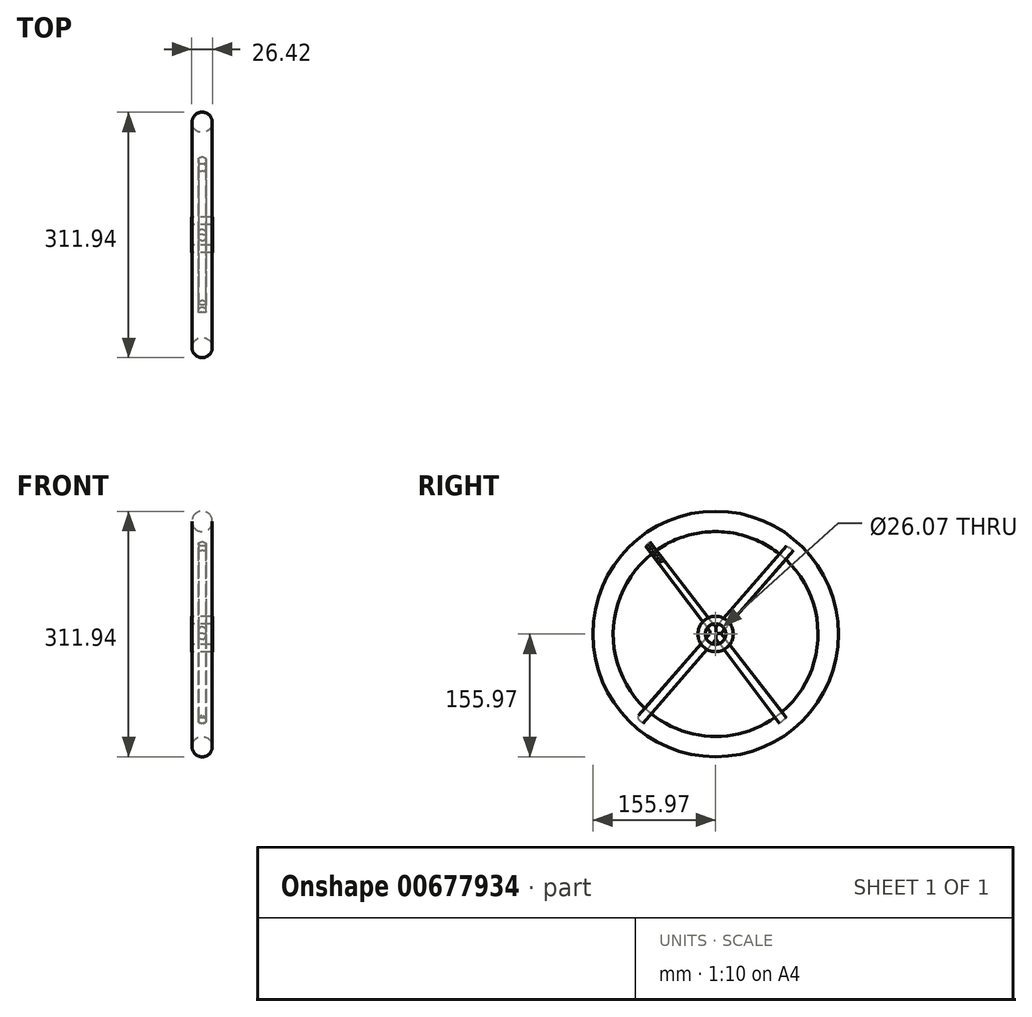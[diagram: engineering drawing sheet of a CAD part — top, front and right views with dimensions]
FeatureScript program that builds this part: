
annotation { "Feature Type Name" : "Feature", "Feature Type Description" : "" }
export const myFeature = defineFeature(function(context is Context, id is Id, definition is map)
    precondition{}
    {
        {
            var Q0;
            Q0=qCreatedBy(makeId("Front.planeOp"),FACE);
            var sketch = newSketch(context, id + "F0", { "sketchPlane" : qUnion([Q0])});
            skLineSegment(sketch, "E0", {"start": v(-177.23, 0) * mm, "end": v(182.9, 0) * mm, "construction": true});
            skCircle(sketch, "E1", {"center": v(0, 143.04) * mm, "radius": 12.92 * mm});
            skSolve(sketch);
        }
        {
            var Q0;
            Q0=makeQuery(id+"F0.imprint","IMPRINT",FACE,{"disambiguationData":[TD([[makeQuery(id+"F0.imprint","IMPRINT",EDGE,{"derivedFrom":sQuery(id+"F0.wireOp",EDGE,"E1")}),1.0]])]});
            var Q1;
            Q1=sQuery(id+"F0.wireOp",EDGE,"E0");
            revolve(context, id + "F1", {"entities" : qUnion([Q0]), "axis" : qUnion([Q1]), "revolveType" : RevolveType.FULL});
        }
        {
            var Q0;
            Q0=qCreatedBy(makeId("Right.planeOp"),FACE);
            var sketch = newSketch(context, id + "F2", { "sketchPlane" : qUnion([Q0])});
            skCircle(sketch, "E2", {"center": v(0, 0) * mm, "radius": 22.46 * mm});
            skCircle(sketch, "E3", {"center": v(0, 0) * mm, "radius": 13.04 * mm});
            skSolve(sketch);
        }
        {
            var Q0;
            Q0 = qSketchRegion(id + "F2", true);
            extrude(context, id + "F3", {"entities" : qUnion([Q0]), "endBound" : BoundingType.SYMMETRIC, "depth" : 26.42 * mm, "offsetDistance" : 25.4 * mm});
        }
        {
            var Q0;
            Q0=qCreatedBy(makeId("Right.planeOp"),FACE);
            var sketch = newSketch(context, id + "F4", { "sketchPlane" : qUnion([Q0])});
            skLineSegment(sketch, "E4", {"start": v(-88.84, 111.85) * mm, "end": v(81, -113.28) * mm});
            skLineSegment(sketch, "E5", {"start": v(81, -113.28) * mm, "end": v(90.1, -106.4) * mm});
            skLineSegment(sketch, "E6", {"start": v(90.1, -106.4) * mm, "end": v(-83.49, 116.85) * mm});
            skLineSegment(sketch, "E7", {"start": v(-83.49, 116.85) * mm, "end": v(-88.84, 111.85) * mm});
            skLineSegment(sketch, "E8", {"start": v(90.1, 111.85) * mm, "end": v(-100.26, -106.4) * mm});
            skLineSegment(sketch, "E9", {"start": v(-100.26, -106.4) * mm, "end": v(-92.37, -113.28) * mm});
            skLineSegment(sketch, "E10", {"start": v(-92.37, -113.28) * mm, "end": v(98.94, 106.05) * mm});
            skLineSegment(sketch, "E11", {"start": v(98.94, 106.05) * mm, "end": v(90.1, 111.85) * mm});
            skSolve(sketch);
        }
        {
            var Q0;
            Q0 = qSketchRegion(id + "F4", true);
            extrude(context, id + "F5", {"entities" : qUnion([Q0]), "endBound" : BoundingType.SYMMETRIC, "depth" : 9.65 * mm, "offsetDistance" : 25.4 * mm});
        }
        {
            var Q0;
            {var subQ0=sQuery(id+"F4.wireOp",EDGE,"E4");Q0=makeQuery(id+"F5.opExtrude","CAP_EDGE",EDGE,{"disambiguationData":[OSD([subQ0]),TDD([makeQuery(id+"F4.imprint","IMPRINT",EDGE,{"disambiguationData":[TD([[makeQuery(id+"F4.imprint","INTERSECT",VERTEX,{"derivedFrom":[subQ0,sQuery(id+"F4.wireOp",EDGE,"E7")]}),-1.0]])],"derivedFrom":subQ0})])],"isStart":false});}
            var Q1;
            {var subQ0=sQuery(id+"F4.wireOp",EDGE,"E4");Q1=makeQuery(id+"F5.opExtrude","CAP_EDGE",EDGE,{"disambiguationData":[OSD([subQ0]),TDD([makeQuery(id+"F4.imprint","IMPRINT",EDGE,{"disambiguationData":[TD([[makeQuery(id+"F4.imprint","INTERSECT",VERTEX,{"derivedFrom":[subQ0,sQuery(id+"F4.wireOp",EDGE,"E7")]}),-1.0]])],"derivedFrom":subQ0})])],"isStart":true});}
            var Q2;
            {var subQ0=sQuery(id+"F4.wireOp",EDGE,"E6");Q2=makeQuery(id+"F5.opExtrude","CAP_EDGE",EDGE,{"disambiguationData":[OSD([subQ0]),TDD([makeQuery(id+"F4.imprint","IMPRINT",EDGE,{"disambiguationData":[TD([[makeQuery(id+"F4.imprint","INTERSECT",VERTEX,{"derivedFrom":[subQ0,sQuery(id+"F4.wireOp",EDGE,"E7")]}),1.0]])],"derivedFrom":subQ0})])],"isStart":false});}
            var Q3;
            {var subQ0=sQuery(id+"F4.wireOp",EDGE,"E6");Q3=makeQuery(id+"F5.opExtrude","CAP_EDGE",EDGE,{"disambiguationData":[OSD([subQ0]),TDD([makeQuery(id+"F4.imprint","IMPRINT",EDGE,{"disambiguationData":[TD([[makeQuery(id+"F4.imprint","INTERSECT",VERTEX,{"derivedFrom":[subQ0,sQuery(id+"F4.wireOp",EDGE,"E7")]}),1.0]])],"derivedFrom":subQ0})])],"isStart":true});}
            var Q4;
            {var subQ0=sQuery(id+"F4.wireOp",EDGE,"E8");Q4=makeQuery(id+"F5.opExtrude","CAP_EDGE",EDGE,{"disambiguationData":[OSD([subQ0]),TDD([makeQuery(id+"F4.imprint","IMPRINT",EDGE,{"disambiguationData":[TD([[makeQuery(id+"F4.imprint","INTERSECT",VERTEX,{"derivedFrom":[subQ0,sQuery(id+"F4.wireOp",EDGE,"E11")]}),-1.0]])],"derivedFrom":subQ0})])],"isStart":false});}
            var Q5;
            {var subQ0=sQuery(id+"F4.wireOp",EDGE,"E8");Q5=makeQuery(id+"F5.opExtrude","CAP_EDGE",EDGE,{"disambiguationData":[OSD([subQ0]),TDD([makeQuery(id+"F4.imprint","IMPRINT",EDGE,{"disambiguationData":[TD([[makeQuery(id+"F4.imprint","INTERSECT",VERTEX,{"derivedFrom":[subQ0,sQuery(id+"F4.wireOp",EDGE,"E11")]}),-1.0]])],"derivedFrom":subQ0})])],"isStart":true});}
            var Q6;
            {var subQ0=sQuery(id+"F4.wireOp",EDGE,"E10");Q6=makeQuery(id+"F5.opExtrude","CAP_EDGE",EDGE,{"disambiguationData":[OSD([subQ0]),TDD([makeQuery(id+"F4.imprint","IMPRINT",EDGE,{"disambiguationData":[TD([[makeQuery(id+"F4.imprint","INTERSECT",VERTEX,{"derivedFrom":[subQ0,sQuery(id+"F4.wireOp",EDGE,"E11")]}),1.0]])],"derivedFrom":subQ0})])],"isStart":false});}
            var Q7;
            {var subQ0=sQuery(id+"F4.wireOp",EDGE,"E10");Q7=makeQuery(id+"F5.opExtrude","CAP_EDGE",EDGE,{"disambiguationData":[OSD([subQ0]),TDD([makeQuery(id+"F4.imprint","IMPRINT",EDGE,{"disambiguationData":[TD([[makeQuery(id+"F4.imprint","INTERSECT",VERTEX,{"derivedFrom":[subQ0,sQuery(id+"F4.wireOp",EDGE,"E11")]}),1.0]])],"derivedFrom":subQ0})])],"isStart":true});}
            var Q8;
            {var subQ0=sQuery(id+"F4.wireOp",EDGE,"E10");Q8=makeQuery(id+"F5.opExtrude","CAP_EDGE",EDGE,{"disambiguationData":[OSD([subQ0]),TDD([makeQuery(id+"F4.imprint","IMPRINT",EDGE,{"disambiguationData":[TD([[makeQuery(id+"F4.imprint","INTERSECT",VERTEX,{"derivedFrom":[sQuery(id+"F4.wireOp",EDGE,"E9"),subQ0]}),-1.0]])],"derivedFrom":subQ0})])],"isStart":true});}
            var Q9;
            {var subQ0=sQuery(id+"F4.wireOp",EDGE,"E10");Q9=makeQuery(id+"F5.opExtrude","CAP_EDGE",EDGE,{"disambiguationData":[OSD([subQ0]),TDD([makeQuery(id+"F4.imprint","IMPRINT",EDGE,{"disambiguationData":[TD([[makeQuery(id+"F4.imprint","INTERSECT",VERTEX,{"derivedFrom":[sQuery(id+"F4.wireOp",EDGE,"E9"),subQ0]}),-1.0]])],"derivedFrom":subQ0})])],"isStart":false});}
            var Q10;
            {var subQ0=sQuery(id+"F4.wireOp",EDGE,"E6");Q10=makeQuery(id+"F5.opExtrude","CAP_EDGE",EDGE,{"disambiguationData":[OSD([subQ0]),TDD([makeQuery(id+"F4.imprint","IMPRINT",EDGE,{"disambiguationData":[TD([[makeQuery(id+"F4.imprint","INTERSECT",VERTEX,{"derivedFrom":[sQuery(id+"F4.wireOp",EDGE,"E5"),subQ0]}),-1.0]])],"derivedFrom":subQ0})])],"isStart":true});}
            var Q11;
            {var subQ0=sQuery(id+"F4.wireOp",EDGE,"E6");Q11=makeQuery(id+"F5.opExtrude","CAP_EDGE",EDGE,{"disambiguationData":[OSD([subQ0]),TDD([makeQuery(id+"F4.imprint","IMPRINT",EDGE,{"disambiguationData":[TD([[makeQuery(id+"F4.imprint","INTERSECT",VERTEX,{"derivedFrom":[sQuery(id+"F4.wireOp",EDGE,"E5"),subQ0]}),-1.0]])],"derivedFrom":subQ0})])],"isStart":false});}
            var Q12;
            {var subQ0=sQuery(id+"F4.wireOp",EDGE,"E4");Q12=makeQuery(id+"F5.opExtrude","CAP_EDGE",EDGE,{"disambiguationData":[OSD([subQ0]),TDD([makeQuery(id+"F4.imprint","IMPRINT",EDGE,{"disambiguationData":[TD([[makeQuery(id+"F4.imprint","INTERSECT",VERTEX,{"derivedFrom":[subQ0,sQuery(id+"F4.wireOp",EDGE,"E5")]}),1.0]])],"derivedFrom":subQ0})])],"isStart":true});}
            var Q13;
            {var subQ0=sQuery(id+"F4.wireOp",EDGE,"E4");Q13=makeQuery(id+"F5.opExtrude","CAP_EDGE",EDGE,{"disambiguationData":[OSD([subQ0]),TDD([makeQuery(id+"F4.imprint","IMPRINT",EDGE,{"disambiguationData":[TD([[makeQuery(id+"F4.imprint","INTERSECT",VERTEX,{"derivedFrom":[subQ0,sQuery(id+"F4.wireOp",EDGE,"E5")]}),1.0]])],"derivedFrom":subQ0})])],"isStart":false});}
            var Q14;
            {var subQ0=sQuery(id+"F4.wireOp",EDGE,"E8");Q14=makeQuery(id+"F5.opExtrude","CAP_EDGE",EDGE,{"disambiguationData":[OSD([subQ0]),TDD([makeQuery(id+"F4.imprint","IMPRINT",EDGE,{"disambiguationData":[TD([[makeQuery(id+"F4.imprint","INTERSECT",VERTEX,{"derivedFrom":[subQ0,sQuery(id+"F4.wireOp",EDGE,"E9")]}),1.0]])],"derivedFrom":subQ0})])],"isStart":true});}
            var Q15;
            {var subQ0=sQuery(id+"F4.wireOp",EDGE,"E8");Q15=makeQuery(id+"F5.opExtrude","SWEPT_FACE",FACE,{"disambiguationData":[OSD([subQ0]),TDD([makeQuery(id+"F4.imprint","IMPRINT",EDGE,{"disambiguationData":[TD([[makeQuery(id+"F4.imprint","INTERSECT",VERTEX,{"derivedFrom":[subQ0,sQuery(id+"F4.wireOp",EDGE,"E9")]}),1.0]])],"derivedFrom":subQ0})])]});}
            fillet(context, id + "F6", {"entities" : qUnion([Q0, Q1, Q2, Q3, Q4, Q5, Q6, Q7, Q8, Q9, Q10, Q11, Q12, Q13, Q14, Q15]), "radius" : 3.86 * mm, "tangentPropagation" : true, "allowEdgeOverflow" : false});
        }
    });
